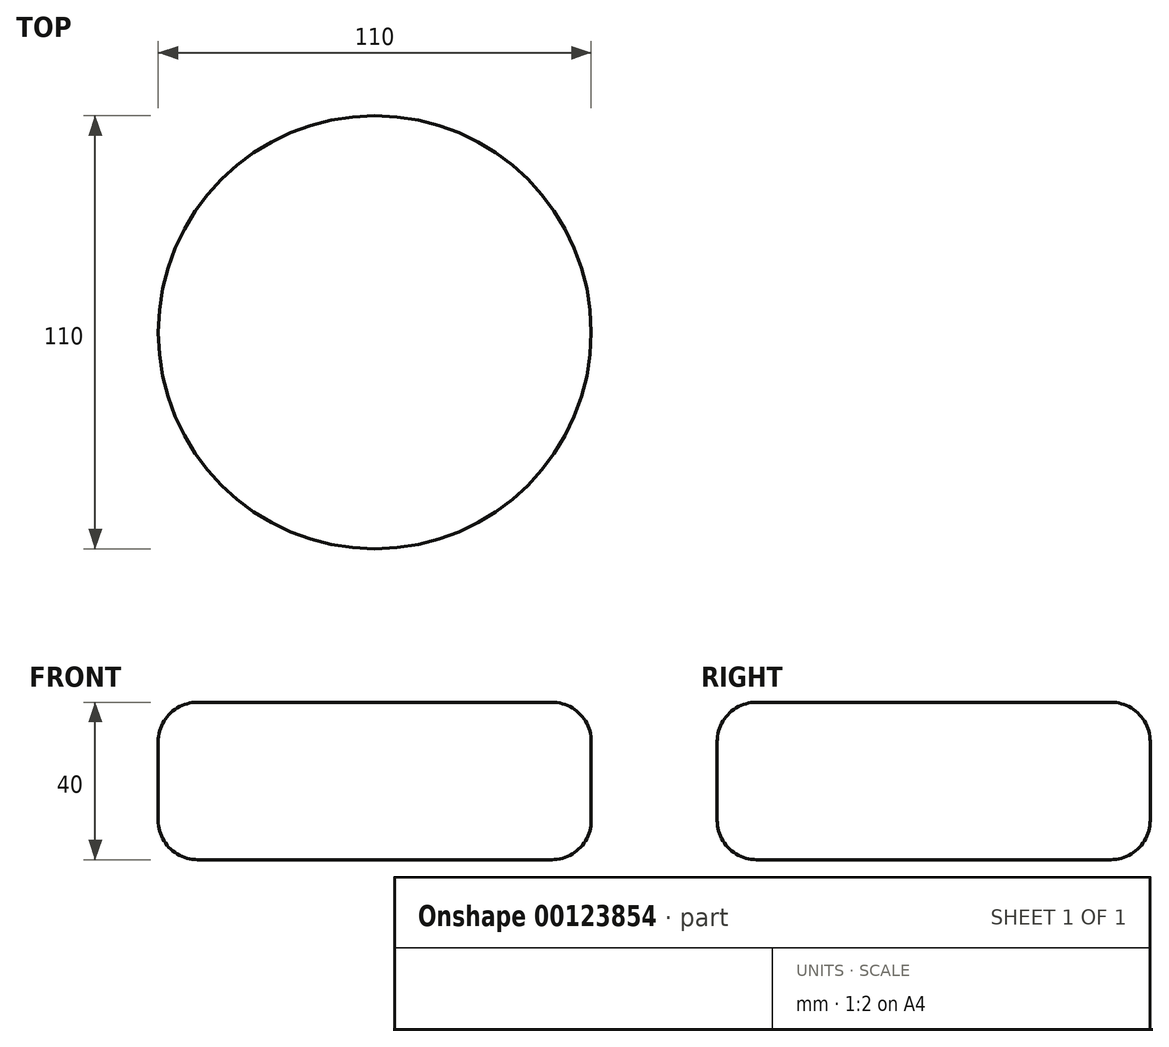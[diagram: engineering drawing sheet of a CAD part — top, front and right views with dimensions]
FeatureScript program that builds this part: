
annotation { "Feature Type Name" : "Feature", "Feature Type Description" : "" }
export const myFeature = defineFeature(function(context is Context, id is Id, definition is map)
    precondition{}
    {
        {
            var Q0;
            Q0=qCreatedBy(makeId("Top.planeOp"),FACE);
            var sketch = newSketch(context, id + "F0", { "sketchPlane" : qUnion([Q0])});
            skCircle(sketch, "E0", {"center": v(0, 0) * mm, "radius": 55 * mm});
            skSolve(sketch);
        }
        {
            var Q0;
            Q0 = qSketchRegion(id + "F0", true);
            extrude(context, id + "F1", {"entities" : qUnion([Q0]), "depth" : 20 * mm, "hasSecondDirection" : true, "secondDirectionOppositeDirection" : true, "secondDirectionDepth" : 20 * mm});
        }
        {
            var Q0;
            Q0=makeQuery(id+"F1.opExtrude","CAP_EDGE",EDGE,{"disambiguationData":[OSD([sQuery(id+"F0.wireOp",EDGE,"E0")])],"isStart":true});
            var Q1;
            Q1=makeQuery(id+"F1.opExtrude","CAP_EDGE",EDGE,{"disambiguationData":[OSD([sQuery(id+"F0.wireOp",EDGE,"E0")])],"isStart":false});
            fillet(context, id + "F2", {"entities" : qUnion([Q0, Q1]), "radius" : 10 * mm, "tangentPropagation" : true, "allowEdgeOverflow" : false});
        }
    });
